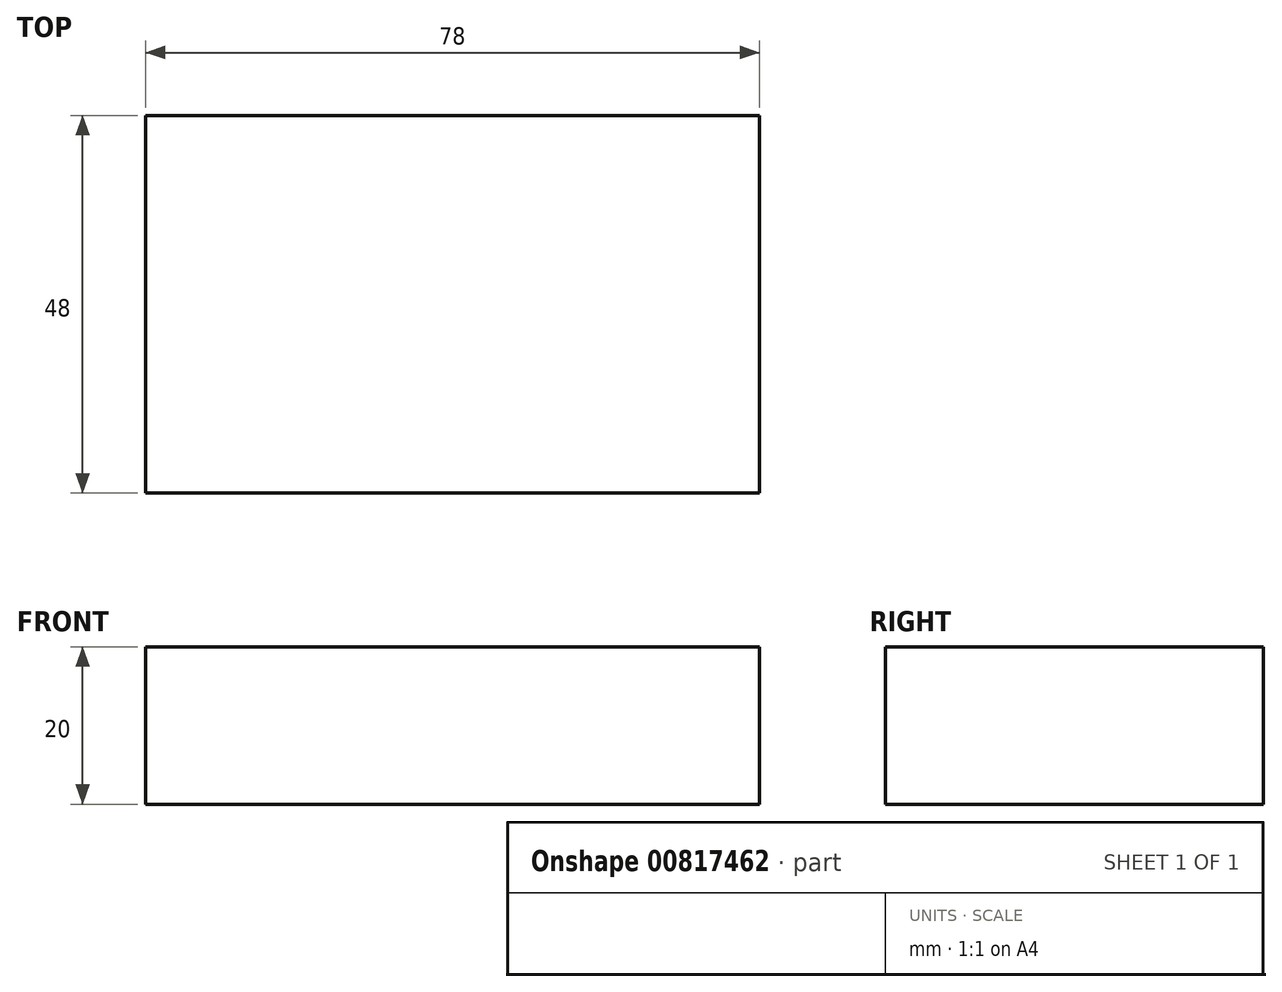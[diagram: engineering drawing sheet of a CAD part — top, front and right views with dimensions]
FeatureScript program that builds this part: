
annotation { "Feature Type Name" : "Feature", "Feature Type Description" : "" }
export const myFeature = defineFeature(function(context is Context, id is Id, definition is map)
    precondition{}
    {
        {
            var Q0;
            Q0=qCreatedBy(makeId("Top.planeOp"),FACE);
            var sketch = newSketch(context, id + "F0", { "sketchPlane" : qUnion([Q0])});
            skLineSegment(sketch, "E0.bottom", {"start": v(39, 24) * mm, "end": v(-39, 24) * mm});
            skLineSegment(sketch, "E0.top", {"start": v(39, -24) * mm, "end": v(-39, -24) * mm});
            skLineSegment(sketch, "E0.left", {"start": v(39, 24) * mm, "end": v(39, -24) * mm});
            skLineSegment(sketch, "E0.right", {"start": v(-39, 24) * mm, "end": v(-39, -24) * mm});
            skPoint(sketch, "E0.middle", {"position": v(0, 0) * mm});
            skSolve(sketch);
        }
        {
            var Q0;
            Q0 = qSketchRegion(id + "F0", true);
            extrude(context, id + "F1", {"entities" : qUnion([Q0]), "depth" : 20 * mm, "offsetDistance" : 25 * mm});
        }
    });
